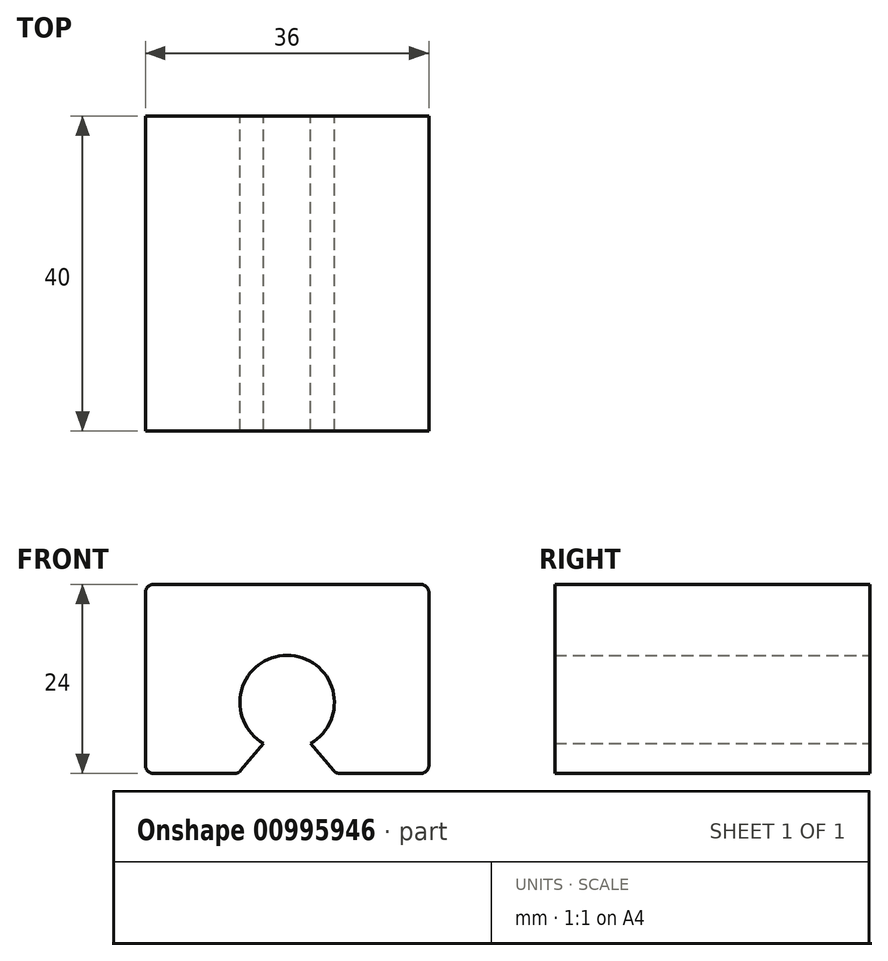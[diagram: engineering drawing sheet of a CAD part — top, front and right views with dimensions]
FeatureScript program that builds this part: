
annotation { "Feature Type Name" : "Feature", "Feature Type Description" : "" }
export const myFeature = defineFeature(function(context is Context, id is Id, definition is map)
    precondition{}
    {
        {
            var Q0;
            Q0=qCreatedBy(makeId("Front.planeOp"),FACE);
            var sketch = newSketch(context, id + "F0", { "sketchPlane" : qUnion([Q0])});
            skLineSegment(sketch, "E0.bottom", {"start": v(-17, -3.8) * mm, "end": v(-6.66, -3.8) * mm});
            skLineSegment(sketch, "E0.top", {"start": v(-17, 20.2) * mm, "end": v(17, 20.2) * mm});
            skLineSegment(sketch, "E0.left", {"start": v(-18, -2.8) * mm, "end": v(-18, 19.2) * mm});
            skLineSegment(sketch, "E0.right", {"start": v(18, -2.8) * mm, "end": v(18, 19.2) * mm});
            skArc(sketch, "E1", {"start": v(3, 0) * mm, "mid": v(0, 11.2) * mm, "end": v(-3, 0) * mm});
            skLineSegment(sketch, "E2", {"start": v(-3, 0) * mm, "end": v(-5.9, -3.45) * mm});
            skLineSegment(sketch, "E3.MirrorCS", {"start": v(3, 0) * mm, "end": v(5.9, -3.45) * mm});
            skPoint(sketch, "E4.visualSharp", {"position": v(-18, 20.2) * mm});
            skArc(sketch, "E4.filletArc", {"start": v(-17, 20.2) * mm, "mid": v(-17.7, 19.9) * mm, "end": v(-18, 19.2) * mm});
            skPoint(sketch, "E5.visualSharp", {"position": v(18, 20.2) * mm});
            skArc(sketch, "E5.filletArc", {"start": v(18, 19.2) * mm, "mid": v(17.7, 19.9) * mm, "end": v(17, 20.2) * mm});
            skPoint(sketch, "E6.visualSharp", {"position": v(-18, -3.8) * mm});
            skArc(sketch, "E6.filletArc", {"start": v(-18, -2.8) * mm, "mid": v(-17.7, -3.51) * mm, "end": v(-17, -3.8) * mm});
            skPoint(sketch, "E7.visualSharp", {"position": v(18, -3.8) * mm});
            skArc(sketch, "E7.filletArc", {"start": v(17, -3.8) * mm, "mid": v(17.7, -3.51) * mm, "end": v(18, -2.8) * mm});
            skPoint(sketch, "E8.newPointB", {"position": v(-6.2, -3.8) * mm});
            skArc(sketch, "E8.filletArc", {"start": v(-6.66, -3.8) * mm, "mid": v(-6.24, -3.71) * mm, "end": v(-5.9, -3.45) * mm});
            skLineSegment(sketch, "E9", {"start": v(17, -3.8) * mm, "end": v(6.66, -3.8) * mm});
            skPoint(sketch, "E10.visualSharp", {"position": v(6.2, -3.8) * mm});
            skArc(sketch, "E10.filletArc", {"start": v(5.9, -3.45) * mm, "mid": v(6.24, -3.71) * mm, "end": v(6.66, -3.8) * mm});
            skSolve(sketch);
        }
        {
            var Q0;
            Q0 = qSketchRegion(id + "F0", true);
            extrude(context, id + "F1", {"entities" : qUnion([Q0]), "depth" : 40 * mm, "offsetDistance" : 25 * mm});
        }
    });
